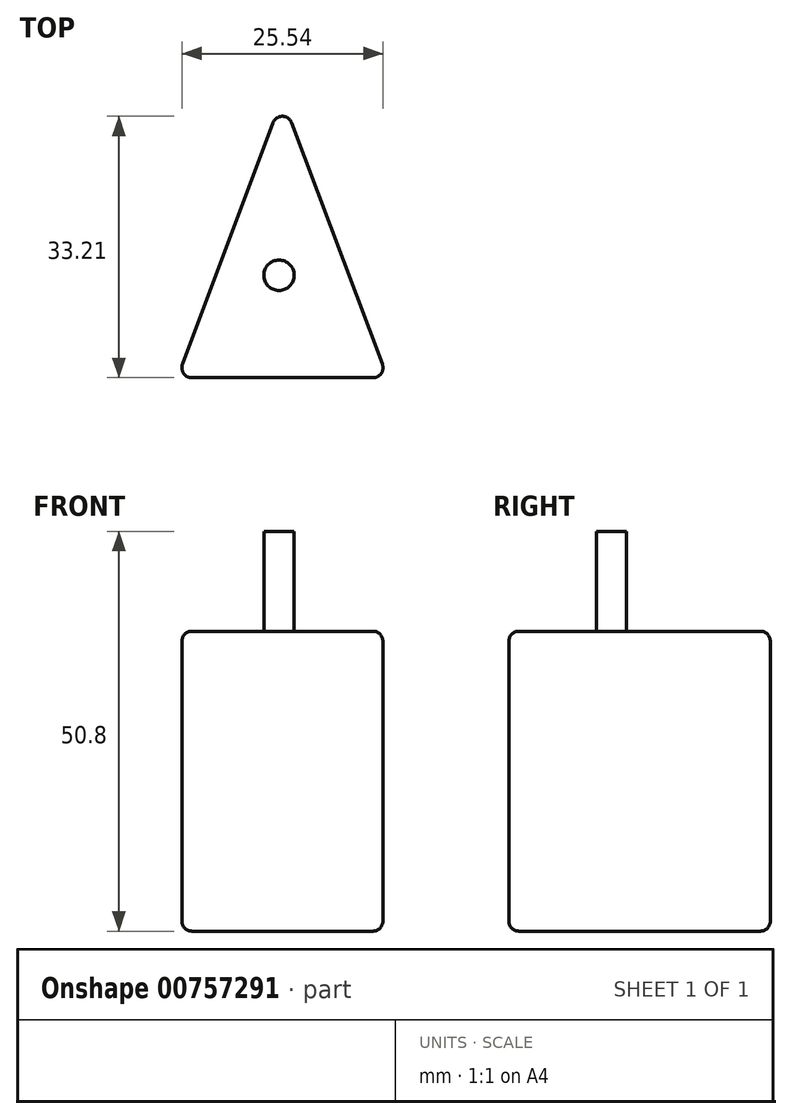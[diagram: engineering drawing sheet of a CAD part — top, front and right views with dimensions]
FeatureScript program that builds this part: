
annotation { "Feature Type Name" : "Feature", "Feature Type Description" : "" }
export const myFeature = defineFeature(function(context is Context, id is Id, definition is map)
    precondition{}
    {
        {
            var Q0;
            Q0=qCreatedBy(makeId("Top.planeOp"),FACE);
            var sketch = newSketch(context, id + "F0", { "sketchPlane" : qUnion([Q0])});
            skLineSegment(sketch, "E0", {"start": v(-14.9, -37.8) * mm, "end": v(11.76, -37.8) * mm});
            skLineSegment(sketch, "E1", {"start": v(-14.9, -37.8) * mm, "end": v(-1.57, -2.25) * mm});
            skLineSegment(sketch, "E2", {"start": v(11.76, -37.8) * mm, "end": v(-1.57, -2.25) * mm});
            skSolve(sketch);
        }
        {
            var Q0;
            Q0 = qSketchRegion(id + "F0", true);
            extrude(context, id + "F1", {"entities" : qUnion([Q0]), "depth" : 38.1 * mm, "offsetDistance" : 25.4 * mm});
        }
        {
            var Q0;
            Q0=qCreatedBy(makeId("Top.planeOp"),FACE);
            var sketch = newSketch(context, id + "F2", { "sketchPlane" : qUnion([Q0])});
            skCircle(sketch, "E3", {"center": v(-2, -24.78) * mm, "radius": 1.93 * mm});
            skSolve(sketch);
        }
        {
            var Q0;
            Q0 = qSketchRegion(id + "F2", true);
            extrude(context, id + "F3", {"entities" : qUnion([Q0]), "operationType" : NewBodyOperationType.ADD, "depth" : 50.8 * mm, "offsetDistance" : 25.4 * mm});
        }
        {
            var Q0;
            Q0=makeQuery(id+"F1.opExtrude","SWEPT_EDGE",EDGE,{"disambiguationData":[OSD([sQuery(id+"F0.wireOp",EDGE,"E1"),sQuery(id+"F0.wireOp",EDGE,"E2")])]});
            var Q1;
            Q1=makeQuery(id+"F1.opExtrude","SWEPT_EDGE",EDGE,{"disambiguationData":[OSD([sQuery(id+"F0.wireOp",EDGE,"E0"),sQuery(id+"F0.wireOp",EDGE,"E2")])]});
            var Q2;
            Q2=makeQuery(id+"F1.opExtrude","SWEPT_EDGE",EDGE,{"disambiguationData":[OSD([sQuery(id+"F0.wireOp",EDGE,"E0"),sQuery(id+"F0.wireOp",EDGE,"E1")])]});
            var Q3;
            Q3=makeQuery(id+"F1.opExtrude","CAP_EDGE",EDGE,{"disambiguationData":[OSD([sQuery(id+"F0.wireOp",EDGE,"E0")])],"isStart":false});
            var Q4;
            Q4=makeQuery(id+"F1.opExtrude","CAP_EDGE",EDGE,{"disambiguationData":[OSD([sQuery(id+"F0.wireOp",EDGE,"E2")])],"isStart":false});
            var Q5;
            Q5=makeQuery(id+"F1.opExtrude","CAP_EDGE",EDGE,{"disambiguationData":[OSD([sQuery(id+"F0.wireOp",EDGE,"E1")])],"isStart":false});
            var Q6;
            Q6=makeQuery(id+"F1.opExtrude","CAP_EDGE",EDGE,{"disambiguationData":[OSD([sQuery(id+"F0.wireOp",EDGE,"E2")])],"isStart":true});
            var Q7;
            Q7=makeQuery(id+"F1.opExtrude","CAP_EDGE",EDGE,{"disambiguationData":[OSD([sQuery(id+"F0.wireOp",EDGE,"E1")])],"isStart":true});
            var Q8;
            Q8=makeQuery(id+"F1.opExtrude","CAP_EDGE",EDGE,{"disambiguationData":[OSD([sQuery(id+"F0.wireOp",EDGE,"E0")])],"isStart":true});
            fillet(context, id + "F4", {"entities" : qUnion([Q0, Q1, Q2, Q3, Q4, Q5, Q6, Q7, Q8]), "radius" : 1.27 * mm, "tangentPropagation" : true, "allowEdgeOverflow" : false});
        }
    });
